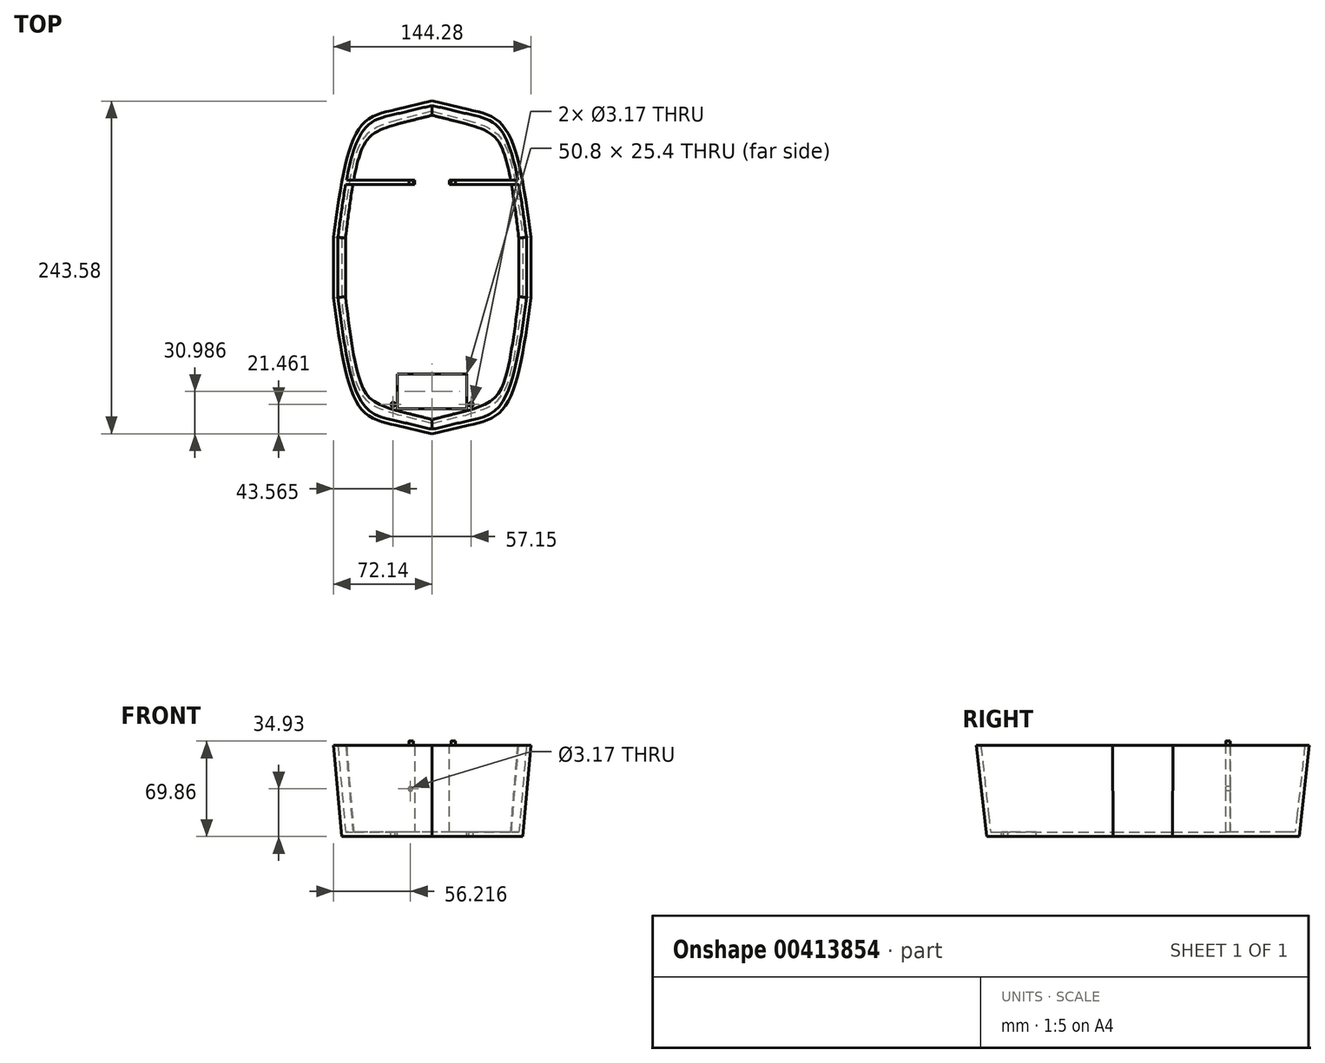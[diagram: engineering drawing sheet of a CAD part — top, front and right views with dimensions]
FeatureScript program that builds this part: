
annotation { "Feature Type Name" : "Feature", "Feature Type Description" : "" }
export const myFeature = defineFeature(function(context is Context, id is Id, definition is map)
    precondition{}
    {
        {
            var Q0;
            Q0=qCreatedBy(makeId("Top.planeOp"),FACE);
            cPlane(context, id + "F0", {"entities" : qUnion([Q0]), "cplaneType" : CPlaneType.OFFSET, "offset" : 53.97 * mm, "width" : 152.4 * mm, "height" : 152.4 * mm});
        }
        {
            var Q0;
            Q0=qCreatedBy(id+"F0.planeOp",FACE);
            var sketch = newSketch(context, id + "F1", { "sketchPlane" : qUnion([Q0])});
            skLineSegment(sketch, "E0", {"start": v(0, 0) * mm, "end": v(0, -114.3) * mm});
            skLineSegment(sketch, "E1", {"start": v(66.31, 0) * mm, "end": v(66.31, -21.67) * mm});
            skLineSegment(sketch, "E2", {"start": v(0, -114.3) * mm, "end": v(24.62, -108.08) * mm});
            skFitSpline(sketch, "E3", {"points": [v(24.62, -108.08) * mm, v(43.46, -100.81) * mm, v(54.7, -86.27) * mm, v(66.31, -21.67) * mm], "startDerivative": vector(76.94, 22.9) * mm, "endDerivative": vector(19.57, 158.53) * mm});
            skLineSegment(sketch, "E4.MirrorCS", {"start": v(66.31, 0) * mm, "end": v(66.31, 21.67) * mm});
            skFitSpline(sketch, "E5.MirrorCS", {"points": [v(24.62, 108.08) * mm, v(43.46, 100.81) * mm, v(54.7, 86.27) * mm, v(66.31, 21.67) * mm], "startDerivative": vector(76.94, -22.9) * mm, "endDerivative": vector(19.57, -158.53) * mm});
            skLineSegment(sketch, "E6.MirrorCS", {"start": v(0, 114.3) * mm, "end": v(24.62, 108.08) * mm});
            skLineSegment(sketch, "E7.MirrorCS", {"start": v(0, 114.3) * mm, "end": v(-24.62, 108.08) * mm});
            skFitSpline(sketch, "E8.MirrorCS", {"points": [v(-24.62, 108.08) * mm, v(-43.46, 100.81) * mm, v(-54.7, 86.27) * mm, v(-66.31, 21.67) * mm], "startDerivative": vector(-76.94, -22.9) * mm, "endDerivative": vector(-19.57, -158.53) * mm});
            skLineSegment(sketch, "E9.MirrorCS", {"start": v(-66.31, 0) * mm, "end": v(-66.31, 21.67) * mm});
            skLineSegment(sketch, "E10.MirrorCS", {"start": v(-66.31, 0) * mm, "end": v(-66.31, -21.67) * mm});
            skFitSpline(sketch, "E11.MirrorCS", {"points": [v(-24.62, -108.08) * mm, v(-43.46, -100.81) * mm, v(-54.7, -86.27) * mm, v(-66.31, -21.67) * mm], "startDerivative": vector(-76.94, 22.9) * mm, "endDerivative": vector(-19.57, 158.53) * mm});
            skLineSegment(sketch, "E12.MirrorCS", {"start": v(0, -114.3) * mm, "end": v(-24.62, -108.08) * mm});
            skLineSegment(sketch, "E13", {"start": v(-66.31, 0) * mm, "end": v(0, 0) * mm});
            skLineSegment(sketch, "E14", {"start": v(0, 0) * mm, "end": v(66.31, 0) * mm});
            skLineSegment(sketch, "E15", {"start": v(0, 0) * mm, "end": v(0, 114.3) * mm});
            skSolve(sketch);
        }
        {
            var Q0;
            Q0=qCreatedBy(id+"F0.planeOp",FACE);
            cPlane(context, id + "F2", {"entities" : qUnion([Q0]), "cplaneType" : CPlaneType.OFFSET, "offset" : 66.67 * mm, "width" : 152.4 * mm, "height" : 152.4 * mm});
        }
        {
            var Q0;
            Q0=qCreatedBy(id+"F2.planeOp",FACE);
            var sketch = newSketch(context, id + "F3", { "sketchPlane" : qUnion([Q0])});
            skLineSegment(sketch, "E16", {"start": v(0, 121.8) * mm, "end": v(26.48, 115.52) * mm});
            skFitSpline(sketch, "E17", {"points": [v(26.48, 115.52) * mm, v(46, 108.9) * mm, v(59.94, 88) * mm, v(72.14, 22.13) * mm], "startDerivative": vector(81.9, -17.1) * mm, "endDerivative": vector(21.27, -161.05) * mm});
            skLineSegment(sketch, "E18", {"start": v(72.14, 22.13) * mm, "end": v(72.14, 0) * mm});
            skLineSegment(sketch, "E19.MirrorCS", {"start": v(0, 121.8) * mm, "end": v(-26.48, 115.52) * mm});
            skFitSpline(sketch, "E20.MirrorCS", {"points": [v(-26.48, 115.52) * mm, v(-46, 108.9) * mm, v(-59.94, 88) * mm, v(-72.14, 22.13) * mm], "startDerivative": vector(-81.9, -17.1) * mm, "endDerivative": vector(-21.27, -161.05) * mm});
            skLineSegment(sketch, "E21.MirrorCS", {"start": v(-72.14, 22.13) * mm, "end": v(-72.14, 0) * mm});
            skLineSegment(sketch, "E22.MirrorCS", {"start": v(72.14, -22.13) * mm, "end": v(72.14, 0) * mm});
            skFitSpline(sketch, "E23.MirrorCS", {"points": [v(26.48, -115.52) * mm, v(46, -108.9) * mm, v(59.94, -88) * mm, v(72.14, -22.13) * mm], "startDerivative": vector(81.9, 17.1) * mm, "endDerivative": vector(21.27, 161.05) * mm});
            skLineSegment(sketch, "E24.MirrorCS", {"start": v(0, -121.8) * mm, "end": v(26.48, -115.52) * mm});
            skLineSegment(sketch, "E25.MirrorCS", {"start": v(0, -121.8) * mm, "end": v(-26.48, -115.52) * mm});
            skFitSpline(sketch, "E26.MirrorCS", {"points": [v(-26.48, -115.52) * mm, v(-46, -108.9) * mm, v(-59.94, -88) * mm, v(-72.14, -22.13) * mm], "startDerivative": vector(-81.9, 17.1) * mm, "endDerivative": vector(-21.27, 161.05) * mm});
            skLineSegment(sketch, "E27.MirrorCS", {"start": v(-72.14, -22.13) * mm, "end": v(-72.14, 0) * mm});
            skLineSegment(sketch, "E28", {"start": v(0, 0) * mm, "end": v(0, -121.8) * mm});
            skLineSegment(sketch, "E29", {"start": v(0, 0) * mm, "end": v(-72.14, 0) * mm});
            skLineSegment(sketch, "E30", {"start": v(0, 0) * mm, "end": v(72.14, 0) * mm});
            skLineSegment(sketch, "E31", {"start": v(0, 0) * mm, "end": v(0, 121.8) * mm});
            skSolve(sketch);
        }
        {
            var Q0;
            Q0=makeQuery(id+"F3.imprint","IMPRINT",FACE,{"disambiguationData":[TD([[makeQuery(id+"F3.imprint","IMPRINT",EDGE,{"derivedFrom":sQuery(id+"F3.wireOp",EDGE,"E25.MirrorCS")}),-1.0]])]});
            var Q1;
            Q1=makeQuery(id+"F1.imprint","IMPRINT",FACE,{"disambiguationData":[TD([[makeQuery(id+"F1.imprint","IMPRINT",EDGE,{"derivedFrom":sQuery(id+"F1.wireOp",EDGE,"E0")}),-1.0]])]});
            loft(context, id + "F4", {"sheetProfilesArray" : [{ "sheetProfileEntities" : qUnion([Q0]) }, { "sheetProfileEntities" : qUnion([Q1]) }]});
        }
        {
            var Q1;
            Q1=makeQuery(id+"F3.imprint","IMPRINT",FACE,{"disambiguationData":[TD([[makeQuery(id+"F3.imprint","IMPRINT",EDGE,{"derivedFrom":sQuery(id+"F3.wireOp",EDGE,"E22.MirrorCS")}),1.0]])]});
            var Q2;
            Q2=makeQuery(id+"F1.imprint","IMPRINT",FACE,{"disambiguationData":[TD([[makeQuery(id+"F1.imprint","IMPRINT",EDGE,{"derivedFrom":sQuery(id+"F1.wireOp",EDGE,"E0")}),1.0]])]});
            loft(context, id + "F5", {"operationType" : NewBodyOperationType.ADD, "sheetProfilesArray" : [{ "sheetProfileEntities" : qUnion([Q1]) }, { "sheetProfileEntities" : qUnion([Q2]) }]});
        }
        {
            var Q1;
            Q1=makeQuery(id+"F3.imprint","IMPRINT",FACE,{"disambiguationData":[TD([[makeQuery(id+"F3.imprint","IMPRINT",EDGE,{"derivedFrom":sQuery(id+"F3.wireOp",EDGE,"E16")}),-1.0]])]});
            var Q2;
            Q2=makeQuery(id+"F1.imprint","IMPRINT",FACE,{"disambiguationData":[TD([[makeQuery(id+"F1.imprint","IMPRINT",EDGE,{"derivedFrom":sQuery(id+"F1.wireOp",EDGE,"E4.MirrorCS")}),1.0]])]});
            loft(context, id + "F6", {"operationType" : NewBodyOperationType.ADD, "sheetProfilesArray" : [{ "sheetProfileEntities" : qUnion([Q1]) }, { "sheetProfileEntities" : qUnion([Q2]) }]});
        }
        {
            var Q1;
            Q1=makeQuery(id+"F3.imprint","IMPRINT",FACE,{"disambiguationData":[TD([[makeQuery(id+"F3.imprint","IMPRINT",EDGE,{"derivedFrom":sQuery(id+"F3.wireOp",EDGE,"E19.MirrorCS")}),1.0]])]});
            var Q2;
            Q2=makeQuery(id+"F1.imprint","IMPRINT",FACE,{"disambiguationData":[TD([[makeQuery(id+"F1.imprint","IMPRINT",EDGE,{"derivedFrom":sQuery(id+"F1.wireOp",EDGE,"E7.MirrorCS")}),1.0]])]});
            loft(context, id + "F7", {"operationType" : NewBodyOperationType.ADD, "sheetProfilesArray" : [{ "sheetProfileEntities" : qUnion([Q1]) }, { "sheetProfileEntities" : qUnion([Q2]) }]});
        }
        {
            var Q0;
            Q0=makeQuery(id+"F7.boolean.opBoolean","MERGE",FACE,{"derivedFrom":[makeQuery(id+"F6.boolean.opBoolean","MERGE",FACE,{"derivedFrom":[makeQuery(id+"F5.boolean.opBoolean","MERGE",FACE,{"derivedFrom":[makeQuery(id+"F4.opLoft","CAP_FACE",FACE,{"disambiguationData":[OSD([makeQuery(id+"F3.imprint","IMPRINT",FACE,{"disambiguationData":[TD([[makeQuery(id+"F3.imprint","IMPRINT",EDGE,{"derivedFrom":sQuery(id+"F3.wireOp",EDGE,"E25.MirrorCS")}),-1.0]])]})])],"isStart":true}),makeQuery(id+"F5.opLoft","CAP_FACE",FACE,{"disambiguationData":[OSD([makeQuery(id+"F3.imprint","IMPRINT",FACE,{"disambiguationData":[TD([[makeQuery(id+"F3.imprint","IMPRINT",EDGE,{"derivedFrom":sQuery(id+"F3.wireOp",EDGE,"E22.MirrorCS")}),1.0]])]})])],"isStart":true})]}),makeQuery(id+"F6.opLoft","CAP_FACE",FACE,{"disambiguationData":[OSD([makeQuery(id+"F3.imprint","IMPRINT",FACE,{"disambiguationData":[TD([[makeQuery(id+"F3.imprint","IMPRINT",EDGE,{"derivedFrom":sQuery(id+"F3.wireOp",EDGE,"E16")}),-1.0]])]})])],"isStart":true})]}),makeQuery(id+"F7.opLoft","CAP_FACE",FACE,{"disambiguationData":[OSD([makeQuery(id+"F3.imprint","IMPRINT",FACE,{"disambiguationData":[TD([[makeQuery(id+"F3.imprint","IMPRINT",EDGE,{"derivedFrom":sQuery(id+"F3.wireOp",EDGE,"E19.MirrorCS")}),1.0]])]})])],"isStart":true})]});
            shell(context, id + "F8", {"entities" : qUnion([Q0]), "thickness" : 3.17 * mm});
        }
        {
            var Q0;
            {var subQ3=makeQuery(id+"F1.imprint","IMPRINT",EDGE,{"derivedFrom":sQuery(id+"F1.wireOp",EDGE,"E0")});Q0=makeQuery(id+"F7.boolean.opBoolean","MERGE",FACE,{"derivedFrom":[makeQuery(id+"F6.boolean.opBoolean","MERGE",FACE,{"derivedFrom":[makeQuery(id+"F5.boolean.opBoolean","MERGE",FACE,{"derivedFrom":[makeQuery(id+"F4.opLoft","CAP_FACE",FACE,{"disambiguationData":[OSD([makeQuery(id+"F1.imprint","IMPRINT",FACE,{"disambiguationData":[TD([[subQ3,-1.0]])]})])],"isStart":true}),makeQuery(id+"F5.opLoft","CAP_FACE",FACE,{"disambiguationData":[OSD([makeQuery(id+"F1.imprint","IMPRINT",FACE,{"disambiguationData":[TD([[subQ3,1.0]])]})])],"isStart":true})]}),makeQuery(id+"F6.opLoft","CAP_FACE",FACE,{"disambiguationData":[OSD([makeQuery(id+"F1.imprint","IMPRINT",FACE,{"disambiguationData":[TD([[makeQuery(id+"F1.imprint","IMPRINT",EDGE,{"derivedFrom":sQuery(id+"F1.wireOp",EDGE,"E4.MirrorCS")}),1.0]])]})])],"isStart":true})]}),makeQuery(id+"F7.opLoft","CAP_FACE",FACE,{"disambiguationData":[OSD([makeQuery(id+"F1.imprint","IMPRINT",FACE,{"disambiguationData":[TD([[makeQuery(id+"F1.imprint","IMPRINT",EDGE,{"derivedFrom":sQuery(id+"F1.wireOp",EDGE,"E7.MirrorCS")}),1.0]])]})])],"isStart":true})]});}
            var sketch = newSketch(context, id + "F9", { "sketchPlane" : qUnion([Q0])});
            skLineSegment(sketch, "E32", {"start": v(-60.38, -63.87) * mm, "end": v(60.38, -63.87) * mm});
            skLineSegment(sketch, "E33.0", {"start": v(-60.38, -60.7) * mm, "end": v(60.38, -60.7) * mm});
            skLineSegment(sketch, "E34", {"start": v(-60.38, -60.7) * mm, "end": v(-60.93, -60.7) * mm});
            skLineSegment(sketch, "E35", {"start": v(-60.93, -60.7) * mm, "end": v(-60.33, -63.87) * mm});
            skLineSegment(sketch, "E36", {"start": v(60.38, -60.7) * mm, "end": v(60.84, -60.7) * mm});
            skLineSegment(sketch, "E37", {"start": v(60.31, -63.87) * mm, "end": v(60.84, -60.7) * mm});
            skSolve(sketch);
        }
        {
            var Q0;
            Q0 = qSketchRegion(id + "F9", true);
            var Q1;
            Q1=makeQuery(id+"F7.boolean.opBoolean","MERGE",FACE,{"derivedFrom":[makeQuery(id+"F6.boolean.opBoolean","MERGE",FACE,{"derivedFrom":[makeQuery(id+"F5.boolean.opBoolean","MERGE",FACE,{"derivedFrom":[makeQuery(id+"F4.opLoft","CAP_FACE",FACE,{"disambiguationData":[OSD([makeQuery(id+"F3.imprint","IMPRINT",FACE,{"disambiguationData":[TD([[makeQuery(id+"F3.imprint","IMPRINT",EDGE,{"derivedFrom":sQuery(id+"F3.wireOp",EDGE,"E25.MirrorCS")}),-1.0]])]})])],"isStart":true}),makeQuery(id+"F5.opLoft","CAP_FACE",FACE,{"disambiguationData":[OSD([makeQuery(id+"F3.imprint","IMPRINT",FACE,{"disambiguationData":[TD([[makeQuery(id+"F3.imprint","IMPRINT",EDGE,{"derivedFrom":sQuery(id+"F3.wireOp",EDGE,"E22.MirrorCS")}),1.0]])]})])],"isStart":true})]}),makeQuery(id+"F6.opLoft","CAP_FACE",FACE,{"disambiguationData":[OSD([makeQuery(id+"F3.imprint","IMPRINT",FACE,{"disambiguationData":[TD([[makeQuery(id+"F3.imprint","IMPRINT",EDGE,{"derivedFrom":sQuery(id+"F3.wireOp",EDGE,"E16")}),-1.0]])]})])],"isStart":true})]}),makeQuery(id+"F7.opLoft","CAP_FACE",FACE,{"disambiguationData":[OSD([makeQuery(id+"F3.imprint","IMPRINT",FACE,{"disambiguationData":[TD([[makeQuery(id+"F3.imprint","IMPRINT",EDGE,{"derivedFrom":sQuery(id+"F3.wireOp",EDGE,"E19.MirrorCS")}),1.0]])]})])],"isStart":true})]});
            extrude(context, id + "F10", {"entities" : qUnion([Q0]), "operationType" : NewBodyOperationType.ADD, "endBound" : BoundingType.UP_TO_SURFACE, "oppositeDirection" : true, "endBoundEntityFace" : qUnion([Q1]), "depth" : 25.4 * mm});
        }
        {
            var Q0;
            Q0=makeQuery(id+"F10.opExtrude","SWEPT_FACE",FACE,{"disambiguationData":[OSD([sQuery(id+"F9.wireOp",EDGE,"E33.0"),sQuery(id+"F9.wireOp",EDGE,"E34"),sQuery(id+"F9.wireOp",EDGE,"E36")])]});
            var sketch = newSketch(context, id + "F11", { "sketchPlane" : qUnion([Q0])});
            skLineSegment(sketch, "E38", {"start": v(0, 57.15) * mm, "end": v(-0.05, 120.65) * mm});
            skLineSegment(sketch, "E39", {"start": v(-0.05, 120.65) * mm, "end": v(-12.75, 120.65) * mm});
            skLineSegment(sketch, "E40", {"start": v(-12.75, 120.65) * mm, "end": v(-12.75, 57.15) * mm});
            skLineSegment(sketch, "E41", {"start": v(-12.75, 57.15) * mm, "end": v(12.65, 57.15) * mm});
            skLineSegment(sketch, "E42", {"start": v(12.65, 57.15) * mm, "end": v(12.65, 92.74) * mm});
            skLineSegment(sketch, "E43", {"start": v(-12.75, 57.15) * mm, "end": v(-15.92, 57.15) * mm});
            skLineSegment(sketch, "E44", {"start": v(-15.92, 57.15) * mm, "end": v(-15.92, 88.9) * mm});
            skCircle(sketch, "E45", {"center": v(-15.92, 88.9) * mm, "radius": 1.59 * mm});
            skLineSegment(sketch, "E46", {"start": v(12.65, 92.74) * mm, "end": v(12.65, 120.65) * mm});
            skLineSegment(sketch, "E47", {"start": v(12.65, 120.65) * mm, "end": v(-0.05, 120.65) * mm});
            skSolve(sketch);
        }
        {
            var Q0;
            Q0 = qSketchRegion(id + "F11", true);
            extrude(context, id + "F12", {"entities" : qUnion([Q0]), "operationType" : NewBodyOperationType.REMOVE, "oppositeDirection" : true, "depth" : 25.4 * mm});
        }
        {
            var Q0;
            Q0=makeQuery(id+"F12.boolean.opBoolean","SPLIT",FACE,{"disambiguationData":[TD([makeQuery(id+"F10.opExtrude","SWEPT_FACE",FACE,{"disambiguationData":[OSD([sQuery(id+"F9.wireOp",EDGE,"E35")])]})])],"derivedFrom":makeQuery(id+"F10.opExtrude","SWEPT_FACE",FACE,{"disambiguationData":[OSD([sQuery(id+"F9.wireOp",EDGE,"E33.0"),sQuery(id+"F9.wireOp",EDGE,"E34"),sQuery(id+"F9.wireOp",EDGE,"E36")])]})});
            var sketch = newSketch(context, id + "F13", { "sketchPlane" : qUnion([Q0])});
            skLineSegment(sketch, "E48", {"start": v(-57.97, 57.15) * mm, "end": v(-65.84, 120.65) * mm});
            skLineSegment(sketch, "E49", {"start": v(-65.84, 120.65) * mm, "end": v(-36.84, 120.65) * mm});
            skLineSegment(sketch, "E50", {"start": v(-36.84, 120.65) * mm, "end": v(-57.97, 57.15) * mm});
            skSolve(sketch);
        }
        {
            var Q0;
            Q0 = qSketchRegion(id + "F13", true);
            extrude(context, id + "F14", {"entities" : qUnion([Q0]), "operationType" : NewBodyOperationType.ADD, "oppositeDirection" : true, "depth" : 3.17 * mm});
        }
        {
            var Q0;
            Q0=makeQuery(id+"F12.boolean.opBoolean","SPLIT",FACE,{"disambiguationData":[TD([makeQuery(id+"F10.opExtrude","SWEPT_FACE",FACE,{"disambiguationData":[OSD([sQuery(id+"F9.wireOp",EDGE,"E37")])]})])],"derivedFrom":makeQuery(id+"F10.opExtrude","SWEPT_FACE",FACE,{"disambiguationData":[OSD([sQuery(id+"F9.wireOp",EDGE,"E33.0"),sQuery(id+"F9.wireOp",EDGE,"E34"),sQuery(id+"F9.wireOp",EDGE,"E36")])]})});
            var sketch = newSketch(context, id + "F15", { "sketchPlane" : qUnion([Q0])});
            skLineSegment(sketch, "E51", {"start": v(57.97, 57.15) * mm, "end": v(64.09, 120.65) * mm});
            skLineSegment(sketch, "E52", {"start": v(64.09, 120.65) * mm, "end": v(46.67, 120.65) * mm});
            skLineSegment(sketch, "E53", {"start": v(46.67, 120.65) * mm, "end": v(57.97, 57.15) * mm});
            skSolve(sketch);
        }
        {
            var Q0;
            Q0 = qSketchRegion(id + "F15", true);
            extrude(context, id + "F16", {"entities" : qUnion([Q0]), "operationType" : NewBodyOperationType.ADD, "oppositeDirection" : true, "depth" : 3.17 * mm});
        }
        {
            var Q0;
            {var subQ5=sQuery(id+"F1.wireOp",EDGE,"E7.MirrorCS");var subQ14=sQuery(id+"F1.wireOp",EDGE,"E4.MirrorCS");var subQ23=sQuery(id+"F1.wireOp",EDGE,"E0");var subQ24=makeQuery(id+"F1.imprint","IMPRINT",EDGE,{"derivedFrom":subQ23});var subQ29=makeQuery(id+"F8.opShell","OFFSET_FACE",FACE,{"disambiguationData":[OSD([makeQuery(id+"F1.imprint","IMPRINT",FACE,{"disambiguationData":[TD([[subQ24,1.0]])]}),makeQuery(id+"F1.imprint","IMPRINT",FACE,{"disambiguationData":[TD([[subQ24,-1.0]])]}),makeQuery(id+"F1.imprint","IMPRINT",FACE,{"disambiguationData":[TD([[makeQuery(id+"F1.imprint","IMPRINT",EDGE,{"derivedFrom":subQ14}),1.0]])]}),makeQuery(id+"F1.imprint","IMPRINT",FACE,{"disambiguationData":[TD([[makeQuery(id+"F1.imprint","IMPRINT",EDGE,{"derivedFrom":subQ5}),1.0]])]})])]});Q0=makeQuery(id+"F12.boolean.opBoolean","MERGE",FACE,{"derivedFrom":[makeQuery(id+"F10.boolean.opBoolean","SPLIT",FACE,{"disambiguationData":[TD([makeQuery(id+"FXR2Hbn0lfyeh1r_1.boolean.opBoolean","COPY",FACE,{"derivedFrom":makeQuery(id+"FXR2Hbn0lfyeh1r_1.opExtrude","SWEPT_FACE",FACE,{"disambiguationData":[OSD([sQuery(id+"FDIKcVqkN8vKakc_1.wireOp",EDGE,"VhtdEZwi-DiHi-E80f-s7wq-SaHQQNDuGKyf")])]})})])],"derivedFrom":subQ29}),makeQuery(id+"F10.boolean.opBoolean","SPLIT",FACE,{"disambiguationData":[TD([makeQuery(id+"F10.opExtrude","SWEPT_FACE",FACE,{"disambiguationData":[OSD([sQuery(id+"F9.wireOp",EDGE,"E32")])]})])],"derivedFrom":subQ29}),makeQuery(id+"F12.opExtrude","SWEPT_FACE",FACE,{"disambiguationData":[OSD([sQuery(id+"F11.wireOp",EDGE,"E41")])]})]});}
            var sketch = newSketch(context, id + "F17", { "sketchPlane" : qUnion([Q0])});
            skLineSegment(sketch, "E54", {"start": v(0, -103.5) * mm, "end": v(-25.4, -103.5) * mm});
            skLineSegment(sketch, "E55", {"start": v(-25.4, -103.5) * mm, "end": v(-25.4, -78.1) * mm});
            skLineSegment(sketch, "E56", {"start": v(-25.4, -78.1) * mm, "end": v(25.4, -78.1) * mm});
            skLineSegment(sketch, "E57", {"start": v(25.4, -78.1) * mm, "end": v(25.4, -103.5) * mm});
            skLineSegment(sketch, "E58", {"start": v(25.4, -103.5) * mm, "end": v(0, -103.5) * mm});
            skLineSegment(sketch, "E59", {"start": v(0, -103.5) * mm, "end": v(0, -100.33) * mm});
            skLineSegment(sketch, "E60", {"start": v(0, -100.33) * mm, "end": v(-28.58, -100.33) * mm});
            skLineSegment(sketch, "E61", {"start": v(0, -100.33) * mm, "end": v(28.58, -100.33) * mm});
            skCircle(sketch, "E62", {"center": v(28.58, -100.33) * mm, "radius": 1.59 * mm});
            skCircle(sketch, "E63", {"center": v(-28.58, -100.33) * mm, "radius": 1.59 * mm});
            skSolve(sketch);
        }
        {
            var Q0;
            Q0 = qSketchRegion(id + "F17", true);
            extrude(context, id + "F18", {"entities" : qUnion([Q0]), "operationType" : NewBodyOperationType.REMOVE, "oppositeDirection" : true, "depth" : 25.4 * mm});
        }
        {
            var Q0;
            {var subQ4=makeQuery(id+"F3.imprint","IMPRINT",FACE,{"disambiguationData":[TD([[makeQuery(id+"F3.imprint","IMPRINT",EDGE,{"derivedFrom":sQuery(id+"F3.wireOp",EDGE,"E25.MirrorCS")}),-1.0]])]});var subQ6=makeQuery(id+"F3.imprint","IMPRINT",FACE,{"disambiguationData":[TD([[makeQuery(id+"F3.imprint","IMPRINT",EDGE,{"derivedFrom":sQuery(id+"F3.wireOp",EDGE,"E22.MirrorCS")}),1.0]])]});var subQ8=makeQuery(id+"F3.imprint","IMPRINT",FACE,{"disambiguationData":[TD([[makeQuery(id+"F3.imprint","IMPRINT",EDGE,{"derivedFrom":sQuery(id+"F3.wireOp",EDGE,"E19.MirrorCS")}),1.0]])]});var subQ9=makeQuery(id+"F3.imprint","IMPRINT",FACE,{"disambiguationData":[TD([[makeQuery(id+"F3.imprint","IMPRINT",EDGE,{"derivedFrom":sQuery(id+"F3.wireOp",EDGE,"E16")}),-1.0]])]});var subQ10=makeQuery(id+"F10.opExtrude","CAP_FACE",FACE,{"disambiguationData":[OSD([subQ9,subQ8,subQ6,subQ4])],"isStart":false});Q0=makeQuery(id+"F16.boolean.opBoolean","MERGE",FACE,{"derivedFrom":[makeQuery(id+"F12.boolean.opBoolean","SPLIT",FACE,{"disambiguationData":[TD([makeQuery(id+"F10.opExtrude","SWEPT_FACE",FACE,{"disambiguationData":[OSD([sQuery(id+"F9.wireOp",EDGE,"E37")])]})])],"derivedFrom":subQ10}),makeQuery(id+"F14.boolean.opBoolean","MERGE",FACE,{"derivedFrom":[makeQuery(id+"F7.boolean.opBoolean","MERGE",FACE,{"derivedFrom":[makeQuery(id+"F6.boolean.opBoolean","MERGE",FACE,{"derivedFrom":[makeQuery(id+"F5.boolean.opBoolean","MERGE",FACE,{"derivedFrom":[makeQuery(id+"F4.opLoft","CAP_FACE",FACE,{"disambiguationData":[OSD([subQ4])],"isStart":true}),makeQuery(id+"F5.opLoft","CAP_FACE",FACE,{"disambiguationData":[OSD([subQ6])],"isStart":true})]}),makeQuery(id+"F6.opLoft","CAP_FACE",FACE,{"disambiguationData":[OSD([subQ9])],"isStart":true})]}),makeQuery(id+"F7.opLoft","CAP_FACE",FACE,{"disambiguationData":[OSD([subQ8])],"isStart":true})]}),makeQuery(id+"F12.boolean.opBoolean","SPLIT",FACE,{"disambiguationData":[TD([makeQuery(id+"F10.opExtrude","SWEPT_FACE",FACE,{"disambiguationData":[OSD([sQuery(id+"F9.wireOp",EDGE,"E35")])]})])],"derivedFrom":subQ10}),makeQuery(id+"F14.opExtrude","SWEPT_FACE",FACE,{"disambiguationData":[OSD([sQuery(id+"F13.wireOp",EDGE,"E49")])]})]}),makeQuery(id+"F16.opExtrude","SWEPT_FACE",FACE,{"disambiguationData":[OSD([sQuery(id+"F15.wireOp",EDGE,"E52")])]})]});}
            var sketch = newSketch(context, id + "F19", { "sketchPlane" : qUnion([Q0])});
            skCircle(sketch, "E64", {"center": v(-15.39, 62.28) * mm, "radius": 1.59 * mm});
            skPoint(sketch, "E64.centerSnap0", {"position": v(-12.75, 62.28) * mm});
            skLineSegment(sketch, "E65", {"start": v(0, 0) * mm, "end": v(0, 35.38) * mm});
            skCircle(sketch, "E66.MirrorC", {"center": v(15.39, 62.28) * mm, "radius": 1.59 * mm});
            skSolve(sketch);
        }
        {
            var Q0;
            Q0 = qSketchRegion(id + "F19", true);
            extrude(context, id + "F20", {"entities" : qUnion([Q0]), "operationType" : NewBodyOperationType.ADD, "depth" : 3.17 * mm});
        }
    });
